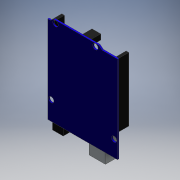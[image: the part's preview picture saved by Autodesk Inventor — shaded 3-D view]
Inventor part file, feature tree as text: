
AUTODESK INVENTOR PART (.ipt)
format: ipt  version: 2016 (Build 200138000, 138)  size: 183,808 bytes
history: native  units: mm
features: extrude x6, sketch x6, other x1
ambient origin geometry x8: Origin, YZ Plane, XZ Plane, XY Plane, X Axis, Y Axis, Z Axis, Center Point
bodies: Body1 (feature_tree)
feature tree (13):
  other  "Sólido1"
  extrude  "Extrusión1"  Depth=8.45mm TaperAngle=0.0deg
  extrude  "Extrusión2"  Depth=10.0mm TaperAngle=0.0deg
  extrude  "Extrusión3"  Depth=12.0mm TaperAngle=0.0deg
  extrude  "Extrusión4"  [1 undecoded]
  extrude  "Extrusión5"  [1 undecoded]
  extrude  "Extrusión6"  [1 undecoded]
  sketch  "Boceto1"  dims[d25=1.0mm d26=0.0mm d39=8.45mm d40=0.0mm]
  sketch  "Boceto2"  dims[d45=8.0mm d46=0.0mm d51=10.0mm d52=0.0mm]
  sketch  "Boceto3"  dims[d57=10.0mm d58=0.0mm d60=12.0mm d61=0.0mm]
  sketch  "Boceto4"
  sketch  "Boceto5"
  sketch  "Boceto6"
note: 3 required parameter values undecoded (feature->parameter linkage not recoverable at this tier; creation-order binding heuristic only, values carry confidence <= 0.55)
